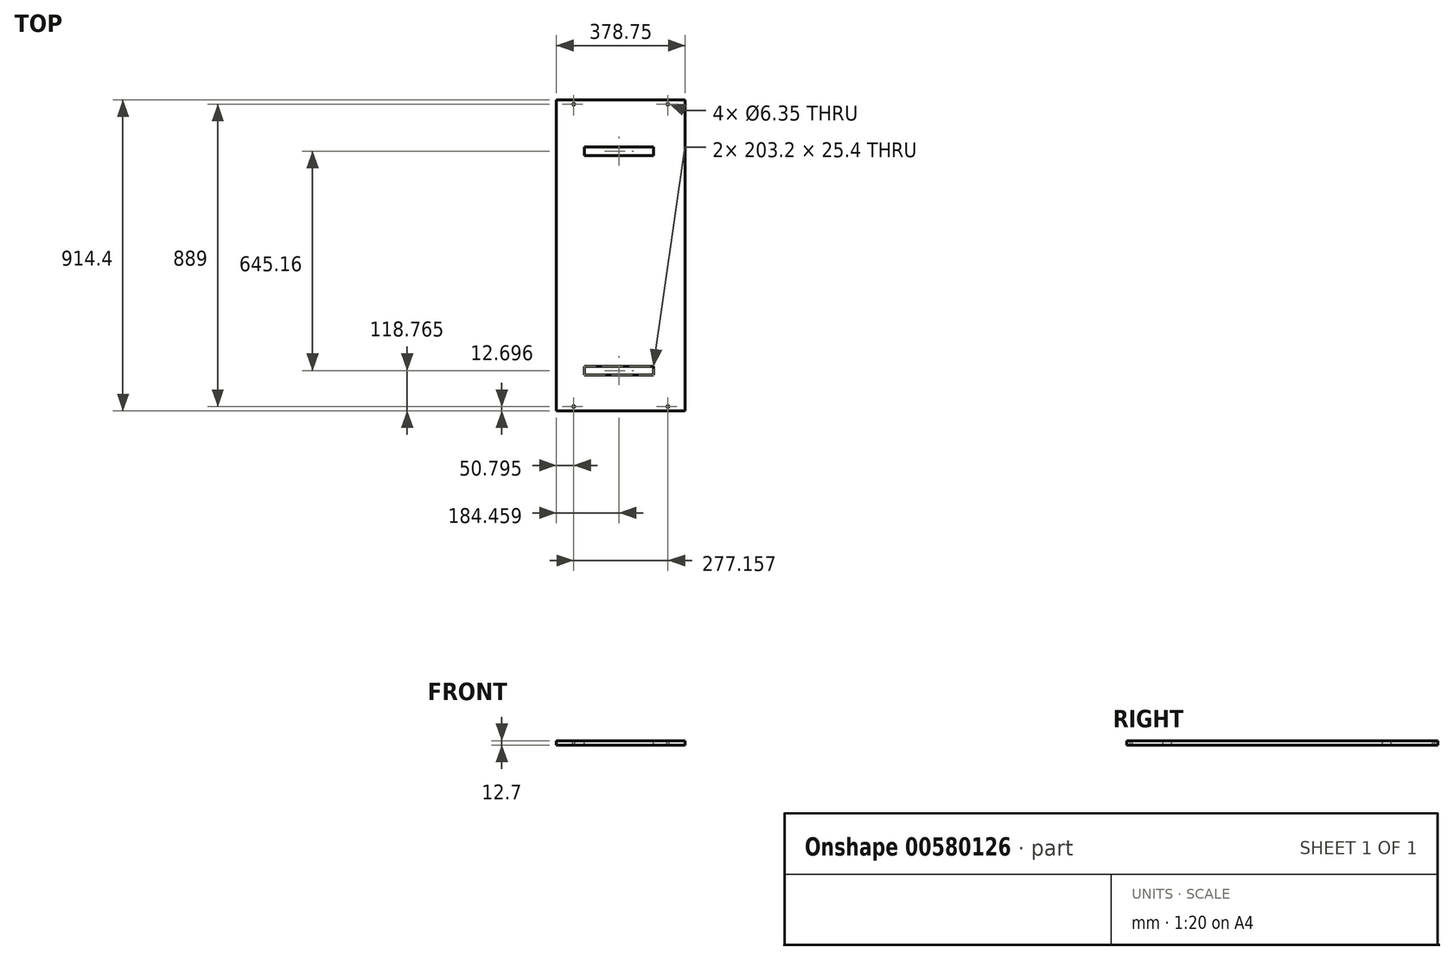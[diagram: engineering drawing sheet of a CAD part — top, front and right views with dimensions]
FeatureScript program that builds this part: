
annotation { "Feature Type Name" : "Feature", "Feature Type Description" : "" }
export const myFeature = defineFeature(function(context is Context, id is Id, definition is map)
    precondition{}
    {
        {
            var Q0;
            Q0=qCreatedBy(makeId("Top.planeOp"),FACE);
            var sketch = newSketch(context, id + "F0", { "sketchPlane" : qUnion([Q0])});
            skLineSegment(sketch, "E0.bottom", {"start": v(185.24, 527.23) * mm, "end": v(-193.51, 527.23) * mm});
            skLineSegment(sketch, "E0.top", {"start": v(185.24, -387.17) * mm, "end": v(-193.51, -387.17) * mm});
            skLineSegment(sketch, "E0.left", {"start": v(185.24, 527.23) * mm, "end": v(185.24, -387.17) * mm});
            skLineSegment(sketch, "E0.right", {"start": v(-193.51, 527.23) * mm, "end": v(-193.51, -387.17) * mm});
            skPoint(sketch, "E0.middle", {"position": v(-4.14, 70.03) * mm});
            skSolve(sketch);
        }
        {
            var Q0;
            Q0=qSketchRegion(id+"F0",true);
            extrude(context, id + "F1", {"entities" : qUnion([Q0]), "depth" : 12.7 * mm, "offsetDistance" : 25.4 * mm});
        }
        {
            var Q0;
            Q0=makeQuery(id+"F1.opExtrude","CAP_FACE",FACE,{"disambiguationData":[OSD([sQuery(id+"F0.wireOp",EDGE,"E0.bottom"),sQuery(id+"F0.wireOp",EDGE,"E0.top"),sQuery(id+"F0.wireOp",EDGE,"E0.left"),sQuery(id+"F0.wireOp",EDGE,"E0.right")])],"isStart":false});
            var sketch = newSketch(context, id + "F2", { "sketchPlane" : qUnion([Q0])});
            skCircle(sketch, "E1", {"center": v(-142.71, 514.53) * mm, "radius": 3.18 * mm});
            skCircle(sketch, "E2", {"center": v(134.44, 514.53) * mm, "radius": 3.17 * mm});
            skCircle(sketch, "E3", {"center": v(-142.71, -374.47) * mm, "radius": 3.17 * mm});
            skCircle(sketch, "E4", {"center": v(134.44, -374.47) * mm, "radius": 3.17 * mm});
            skLineSegment(sketch, "E5", {"start": v(-142.71, 527.23) * mm, "end": v(-142.71, 514.53) * mm});
            skLineSegment(sketch, "E6", {"start": v(-142.71, 511.35) * mm, "end": v(-142.71, 514.53) * mm});
            skLineSegment(sketch, "E7", {"start": v(134.44, 514.53) * mm, "end": v(134.44, 527.23) * mm});
            skLineSegment(sketch, "E8", {"start": v(134.44, 514.53) * mm, "end": v(134.44, 511.35) * mm});
            skLineSegment(sketch, "E9", {"start": v(134.44, -371.3) * mm, "end": v(134.44, -374.47) * mm});
            skLineSegment(sketch, "E10", {"start": v(134.44, -387.17) * mm, "end": v(134.44, -374.47) * mm});
            skLineSegment(sketch, "E11", {"start": v(-142.71, -374.47) * mm, "end": v(-142.71, -377.65) * mm});
            skLineSegment(sketch, "E12", {"start": v(-142.71, -377.65) * mm, "end": v(-142.71, -387.17) * mm});
            skSolve(sketch);
        }
        {
            var Q0;
            Q0=qSketchRegion(id+"F2",true);
            extrude(context, id + "F3", {"entities" : qUnion([Q0]), "operationType" : NewBodyOperationType.REMOVE, "endBound" : BoundingType.THROUGH_ALL, "oppositeDirection" : true, "depth" : 25.4 * mm, "offsetDistance" : 25.4 * mm});
        }
        {
            var Q0;
            Q0=makeQuery(id+"F1.opExtrude","CAP_FACE",FACE,{"disambiguationData":[OSD([sQuery(id+"F0.wireOp",EDGE,"E0.bottom"),sQuery(id+"F0.wireOp",EDGE,"E0.top"),sQuery(id+"F0.wireOp",EDGE,"E0.left"),sQuery(id+"F0.wireOp",EDGE,"E0.right")])],"isStart":false});
            var sketch = newSketch(context, id + "F4", { "sketchPlane" : qUnion([Q0])});
            skLineSegment(sketch, "E13.bottom", {"start": v(92.55, 364.05) * mm, "end": v(-110.65, 364.05) * mm});
            skLineSegment(sketch, "E13.top", {"start": v(92.55, 389.45) * mm, "end": v(-110.65, 389.45) * mm});
            skLineSegment(sketch, "E13.left", {"start": v(92.55, 364.05) * mm, "end": v(92.55, 389.45) * mm});
            skLineSegment(sketch, "E13.right", {"start": v(-110.65, 364.05) * mm, "end": v(-110.65, 389.45) * mm});
            skPoint(sketch, "E13.middle", {"position": v(-9.05, 376.75) * mm});
            skLineSegment(sketch, "E14.bottom", {"start": v(92.55, -281.1) * mm, "end": v(-110.65, -281.1) * mm});
            skLineSegment(sketch, "E14.top", {"start": v(92.55, -255.7) * mm, "end": v(-110.65, -255.7) * mm});
            skLineSegment(sketch, "E14.left", {"start": v(92.55, -281.1) * mm, "end": v(92.55, -255.7) * mm});
            skLineSegment(sketch, "E14.right", {"start": v(-110.65, -281.1) * mm, "end": v(-110.65, -255.7) * mm});
            skPoint(sketch, "E14.middle", {"position": v(-9.05, -268.4) * mm});
            skSolve(sketch);
        }
        {
            var Q0;
            Q0=qSketchRegion(id+"F4",true);
            extrude(context, id + "F5", {"entities" : qUnion([Q0]), "operationType" : NewBodyOperationType.REMOVE, "oppositeDirection" : true, "depth" : 25.4 * mm, "offsetDistance" : 25.4 * mm});
        }
    });
